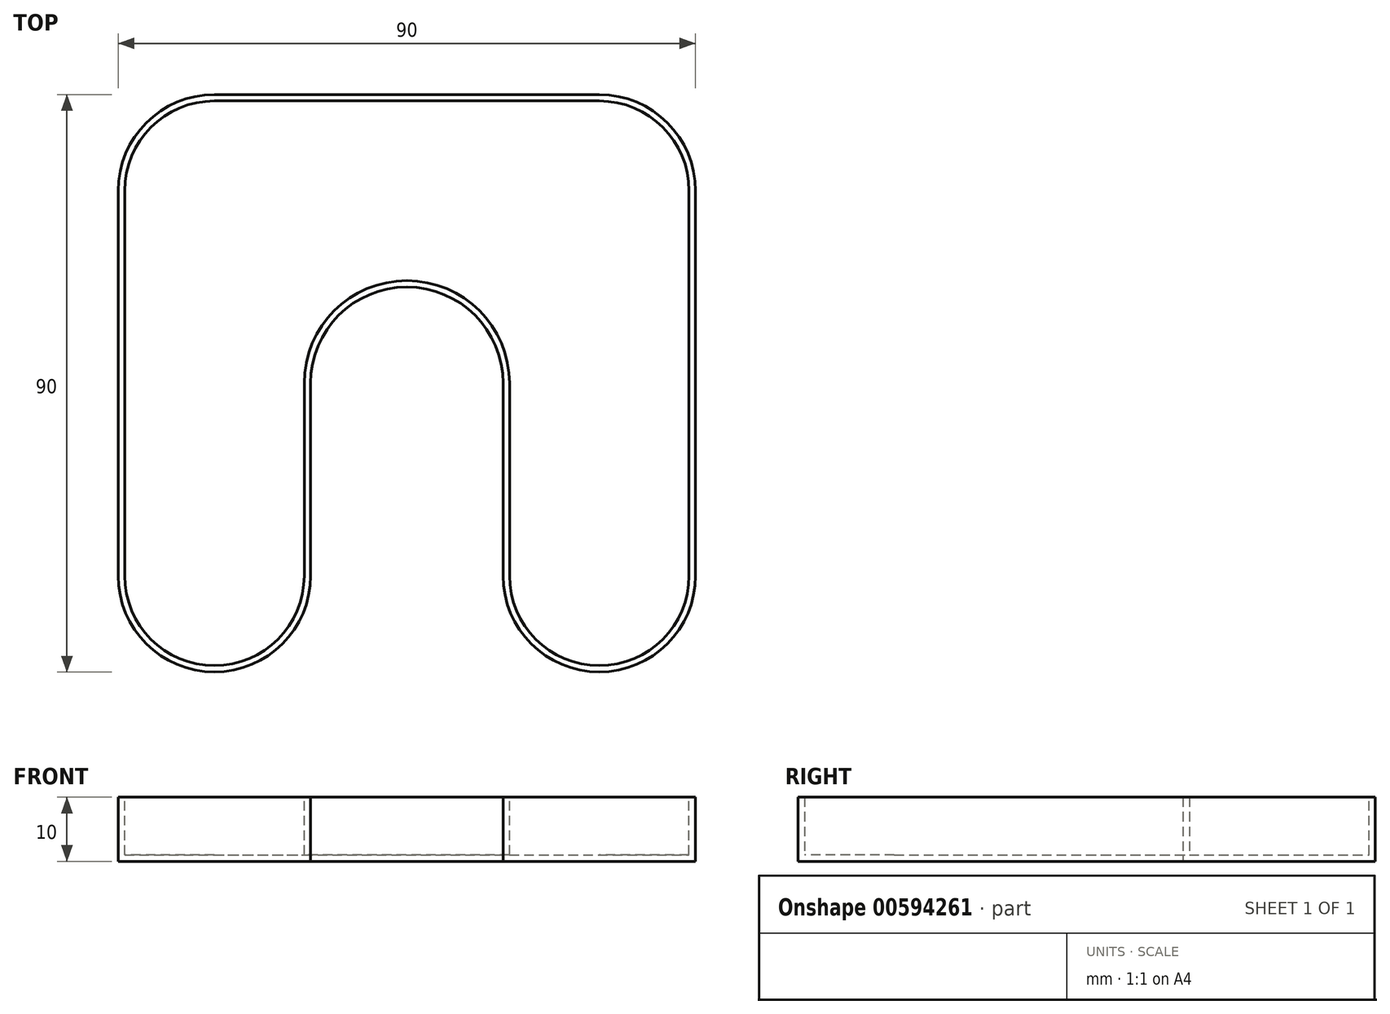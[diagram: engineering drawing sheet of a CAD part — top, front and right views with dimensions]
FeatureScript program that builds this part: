
annotation { "Feature Type Name" : "Feature", "Feature Type Description" : "" }
export const myFeature = defineFeature(function(context is Context, id is Id, definition is map)
    precondition{}
    {
        {
            var Q0;
            Q0=qCreatedBy(makeId("Top.planeOp"),FACE);
            var sketch = newSketch(context, id + "F0", { "sketchPlane" : qUnion([Q0])});
            skLineSegment(sketch, "E0.bottom", {"start": v(15, 0) * mm, "end": v(15, 0) * mm});
            skLineSegment(sketch, "E0.top", {"start": v(15, 90) * mm, "end": v(75, 90) * mm});
            skLineSegment(sketch, "E0.left", {"start": v(0, 15) * mm, "end": v(0, 75) * mm});
            skLineSegment(sketch, "E0.right", {"start": v(90, 15) * mm, "end": v(90, 75) * mm});
            skLineSegment(sketch, "E1.bottom", {"start": v(30, 0) * mm, "end": v(60, 0) * mm});
            skLineSegment(sketch, "E1.top", {"start": v(45, 60) * mm, "end": v(45, 60) * mm});
            skLineSegment(sketch, "E1.left", {"start": v(30, 15) * mm, "end": v(30, 45) * mm});
            skLineSegment(sketch, "E1.right", {"start": v(60, 15) * mm, "end": v(60, 45) * mm});
            skPoint(sketch, "E2.visualSharp", {"position": v(0, 90) * mm});
            skArc(sketch, "E2.filletArc", {"start": v(15, 90) * mm, "mid": v(4.4, 85.6) * mm, "end": v(0, 75) * mm});
            skPoint(sketch, "E3.visualSharp", {"position": v(90, 90) * mm});
            skArc(sketch, "E3.filletArc", {"start": v(90, 75) * mm, "mid": v(85.6, 85.6) * mm, "end": v(75, 90) * mm});
            skPoint(sketch, "E4.visualSharp", {"position": v(0, 0) * mm});
            skArc(sketch, "E4.filletArc", {"start": v(0, 15) * mm, "mid": v(4.4, 4.4) * mm, "end": v(15, 0) * mm});
            skPoint(sketch, "E5.newPointB", {"position": v(30, 0) * mm});
            skArc(sketch, "E5.filletArc", {"start": v(15, 0) * mm, "mid": v(25.6, 4.4) * mm, "end": v(30, 15) * mm});
            skLineSegment(sketch, "E6", {"start": v(75, 0) * mm, "end": v(75, 0) * mm});
            skPoint(sketch, "E7.visualSharp", {"position": v(60, 0) * mm});
            skArc(sketch, "E7.filletArc", {"start": v(60, 15) * mm, "mid": v(64.4, 4.4) * mm, "end": v(75, 0) * mm});
            skPoint(sketch, "E8.visualSharp", {"position": v(90, 0) * mm});
            skArc(sketch, "E8.filletArc", {"start": v(75, 0) * mm, "mid": v(85.6, 4.4) * mm, "end": v(90, 15) * mm});
            skPoint(sketch, "E9.visualSharp", {"position": v(30, 60) * mm});
            skArc(sketch, "E9.filletArc", {"start": v(45, 60) * mm, "mid": v(34.4, 55.6) * mm, "end": v(30, 45) * mm});
            skPoint(sketch, "E10.visualSharp", {"position": v(60, 60) * mm});
            skArc(sketch, "E10.filletArc", {"start": v(60, 45) * mm, "mid": v(55.6, 55.6) * mm, "end": v(45, 60) * mm});
            skSolve(sketch);
        }
        {
            var Q0;
            Q0=makeQuery(id+"F0.imprint","IMPRINT",FACE,{"disambiguationData":[TD([[makeQuery(id+"F0.imprint","IMPRINT",EDGE,{"derivedFrom":sQuery(id+"F0.wireOp",EDGE,"E0.top")}),-1.0]])]});
            extrude(context, id + "F1", {"entities" : qUnion([Q0]), "depth" : 10 * mm, "offsetDistance" : 25 * mm});
        }
        {
            var Q0;
            Q0=makeQuery(id+"F1.opExtrude","CAP_FACE",FACE,{"disambiguationData":[OSD([sQuery(id+"F0.wireOp",EDGE,"E0.top"),sQuery(id+"F0.wireOp",EDGE,"E0.left"),sQuery(id+"F0.wireOp",EDGE,"E0.right"),sQuery(id+"F0.wireOp",EDGE,"E1.left"),sQuery(id+"F0.wireOp",EDGE,"E1.right"),sQuery(id+"F0.wireOp",EDGE,"E2.filletArc"),sQuery(id+"F0.wireOp",EDGE,"E3.filletArc"),sQuery(id+"F0.wireOp",EDGE,"E4.filletArc"),sQuery(id+"F0.wireOp",EDGE,"E5.filletArc"),sQuery(id+"F0.wireOp",EDGE,"E7.filletArc"),sQuery(id+"F0.wireOp",EDGE,"E8.filletArc"),sQuery(id+"F0.wireOp",EDGE,"E9.filletArc"),sQuery(id+"F0.wireOp",EDGE,"E10.filletArc")])],"isStart":false});
            shell(context, id + "F2", {"entities" : qUnion([Q0]), "thickness" : 1 * mm});
        }
    });
